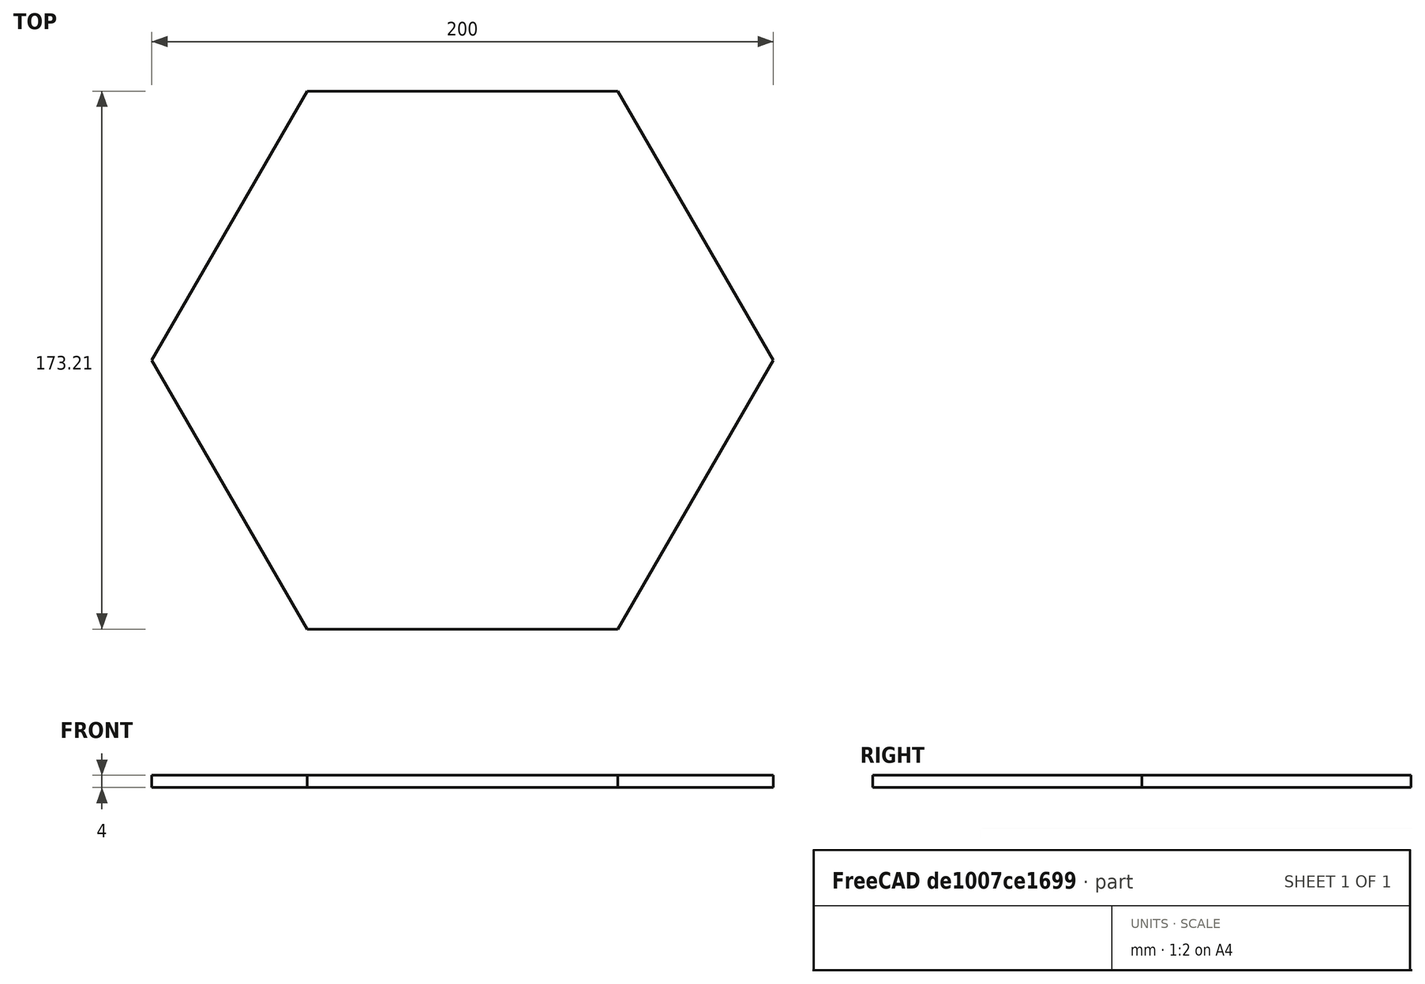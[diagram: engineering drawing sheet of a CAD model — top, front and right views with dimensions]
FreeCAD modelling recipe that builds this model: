
FCSTD DOCUMENT  (FreeCAD 0.18R4 (GitTag))
Label: Bottom
License: All rights reserved
LicenseURL: http://en.wikipedia.org/wiki/All_rights_reserved
objects: Sketcher::SketchObject×1, PartDesign::Pad×1, PartDesign::Body×1, App::MeasureDistance×1
note: 4 computed .brp shape members not serialized (recipe doc carries the construction recipe); baked Part::Feature solids carry a one-line shape summary decoded from their .brp

FEATURE [Sketcher::SketchObject] Sketch
  MapMode = 5
  Support = -> [XY_Plane]
  sketch-geometry (7):
    g0: LineSegment StartX=-50 StartY=0 StartZ=0 EndX=0 EndY=86.6025 EndZ=0
    g1: LineSegment StartX=0 StartY=86.6025 StartZ=0 EndX=-50 EndY=173.205 EndZ=0
    g2: LineSegment StartX=-50 StartY=173.205 StartZ=0 EndX=-150 EndY=173.205 EndZ=0
    g3: LineSegment StartX=-150 StartY=173.205 StartZ=0 EndX=-200 EndY=86.6025 EndZ=0
    g4: LineSegment StartX=-200 StartY=86.6025 StartZ=0 EndX=-150 EndY=0 EndZ=0
    g5: LineSegment StartX=-150 StartY=0 StartZ=0 EndX=-50 EndY=0 EndZ=0
    g6: Circle [constr] CenterX=-100 CenterY=86.6025 CenterZ=0 NormalX=0 NormalY=0 NormalZ=1 AngleXU=0 Radius=100
  constraints (17):
    c: Coincident(g0,g1)
    c: Coincident(g1,g2)
    c: Coincident(g2,g3)
    c: Coincident(g3,g4)
    c: Coincident(g4,g5)
    c: Coincident(g5,g0)
    c: Equal(g0, g1-g5) x5
    c: PointOnObject(g0,g6)
    c: PointOnObject(g1,g6)
    c: PointOnObject(g2,g6)
    c: PointOnObject(g3,g6)
    c: PointOnObject(g4,g6)
    c: PointOnObject(g5,g6)
    c: PointOnObject(g0,g-2)
    c: PointOnObject(g0,g-1)
    c: PointOnObject(g4,g-1)
    c: DistanceX(g5,g5) = 100
FEATURE [PartDesign::Pad] Pad
  Length = 4
  Length2 = 100
  Profile = -> Sketch
  Type = 0
FEATURE [PartDesign::Body] Body
  Group = -> [Sketch,Pad]
  Origin = -> Origin
  Tip = -> Pad
FEATURE [App::MeasureDistance] Distance  label="Distance: 200,00 mm"
  Distance = 200
  P1 = (-200,86.6025,4)
  P2 = (0,86.6025,4)
